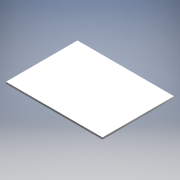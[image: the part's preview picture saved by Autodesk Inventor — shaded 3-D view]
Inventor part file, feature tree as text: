
AUTODESK INVENTOR PART (.ipt)
format: ipt  version: 2019 (Build 230136000, 136)  size: 90,624 bytes
history: native  units: mm
features: extrude x1, sketch x1
ambient origin geometry x8: Origin, YZ Plane, XZ Plane, XY Plane, X Axis, Y Axis, Z Axis, Center Point
bodies: Solid1 (feature_tree)
feature tree (2):
  extrude  "Extrusion1"  Depth=200.0mm
  sketch  "Sketch1"  dims[d0=270.0mm d1=200.0mm d2=5.0mm d3=0.0mm]
